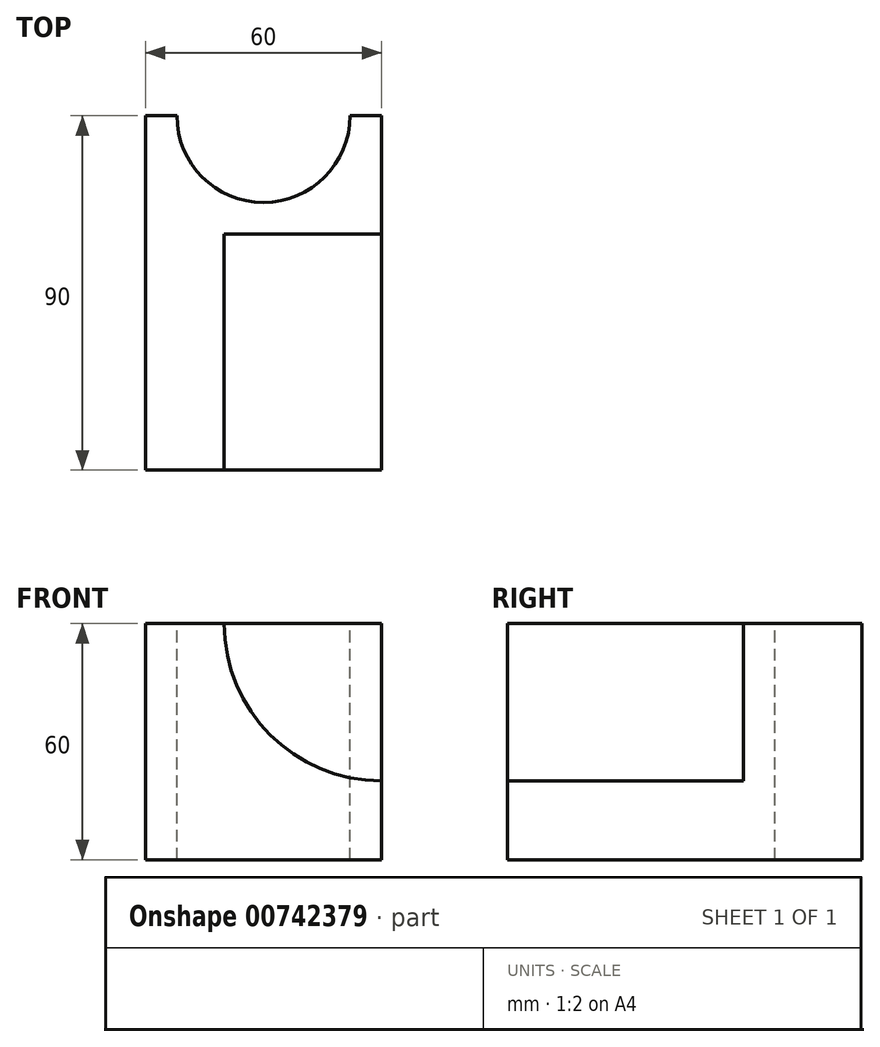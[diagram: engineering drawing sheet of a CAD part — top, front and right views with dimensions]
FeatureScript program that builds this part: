
annotation { "Feature Type Name" : "Feature", "Feature Type Description" : "" }
export const myFeature = defineFeature(function(context is Context, id is Id, definition is map)
    precondition{}
    {
        {
            var Q0;
            Q0=qCreatedBy(makeId("Front.planeOp"),FACE);
            var sketch = newSketch(context, id + "F0", { "sketchPlane" : qUnion([Q0])});
            skLineSegment(sketch, "E0", {"start": v(-20, 0) * mm, "end": v(0, 0) * mm});
            skArc(sketch, "E1", {"start": v(0, 0) * mm, "mid": v(11.72, -28.28) * mm, "end": v(40, -40) * mm});
            skLineSegment(sketch, "E2", {"start": v(-20, 0) * mm, "end": v(-20, -60) * mm});
            skLineSegment(sketch, "E3", {"start": v(-20, -60) * mm, "end": v(40, -60) * mm});
            skLineSegment(sketch, "E4", {"start": v(40, -60) * mm, "end": v(40, -40) * mm});
            skLineSegment(sketch, "E5", {"start": v(0, 0) * mm, "end": v(40, 0) * mm});
            skLineSegment(sketch, "E6", {"start": v(40, 0) * mm, "end": v(40, -40) * mm});
            skLineSegment(sketch, "E7", {"start": v(-20, 0) * mm, "end": v(40, 0) * mm});
            skSolve(sketch);
        }
        {
            var Q0;
            {var subQ0=makeQuery(id+"F0.imprint","IMPRINT",EDGE,{"derivedFrom":sQuery(id+"F0.wireOp",EDGE,"E1")});Q0=qUnion([makeQuery(id+"F0.imprint","IMPRINT",FACE,{"disambiguationData":[TD([[makeQuery(id+"F0.imprint","IMPRINT",EDGE,{"derivedFrom":sQuery(id+"F0.wireOp",EDGE,"E0")}),-1.0]])]}),makeQuery(id+"F0.imprint","IMPRINT",FACE,{"disambiguationData":[TD([[subQ0,1.0]])]})]);}
            extrude(context, id + "F1", {"entities" : qUnion([Q0]), "oppositeDirection" : true, "depth" : 90 * mm, "offsetDistance" : 25 * mm});
        }
        {
            var Q0;
            Q0=makeQuery(id+"F0.imprint","IMPRINT",FACE,{"disambiguationData":[TD([[makeQuery(id+"F0.imprint","IMPRINT",EDGE,{"derivedFrom":sQuery(id+"F0.wireOp",EDGE,"E1")}),1.0]])]});
            extrude(context, id + "F2", {"entities" : qUnion([Q0]), "operationType" : NewBodyOperationType.REMOVE, "oppositeDirection" : true, "depth" : 60 * mm, "offsetDistance" : 25 * mm});
        }
        {
            var Q0;
            Q0=makeQuery(id+"F1.opExtrude","SWEPT_FACE",FACE,{"disambiguationData":[OSD([sQuery(id+"F0.wireOp",EDGE,"E0"),sQuery(id+"F0.wireOp",EDGE,"E5")])]});
            var sketch = newSketch(context, id + "F3", { "sketchPlane" : qUnion([Q0])});
            skLineSegment(sketch, "E8", {"start": v(-20, 0) * mm, "end": v(40, 0) * mm});
            skLineSegment(sketch, "E9", {"start": v(40, 0) * mm, "end": v(40, 90) * mm});
            skLineSegment(sketch, "E10", {"start": v(40, 90) * mm, "end": v(-20, 90) * mm});
            skLineSegment(sketch, "E11", {"start": v(-20, 90) * mm, "end": v(-20, 0) * mm});
            skPoint(sketch, "E12", {"position": v(10, 90) * mm});
            skArc(sketch, "E13", {"start": v(-12, 90) * mm, "mid": v(10, 68) * mm, "end": v(32, 90) * mm});
            skSolve(sketch);
        }
        {
            var Q0;
            {var subQ0=sQuery(id+"F3.wireOp",EDGE,"E13");Q0=makeQuery(id+"F3.imprint","IMPRINT",FACE,{"disambiguationData":[TD([[makeQuery(id+"F3.imprint","IMPRINT",EDGE,{"derivedFrom":subQ0}),1.0]])]});}
            extrude(context, id + "F4", {"entities" : qUnion([Q0]), "operationType" : NewBodyOperationType.REMOVE, "endBound" : BoundingType.THROUGH_ALL, "oppositeDirection" : true, "depth" : 25 * mm, "offsetDistance" : 25 * mm});
        }
    });
